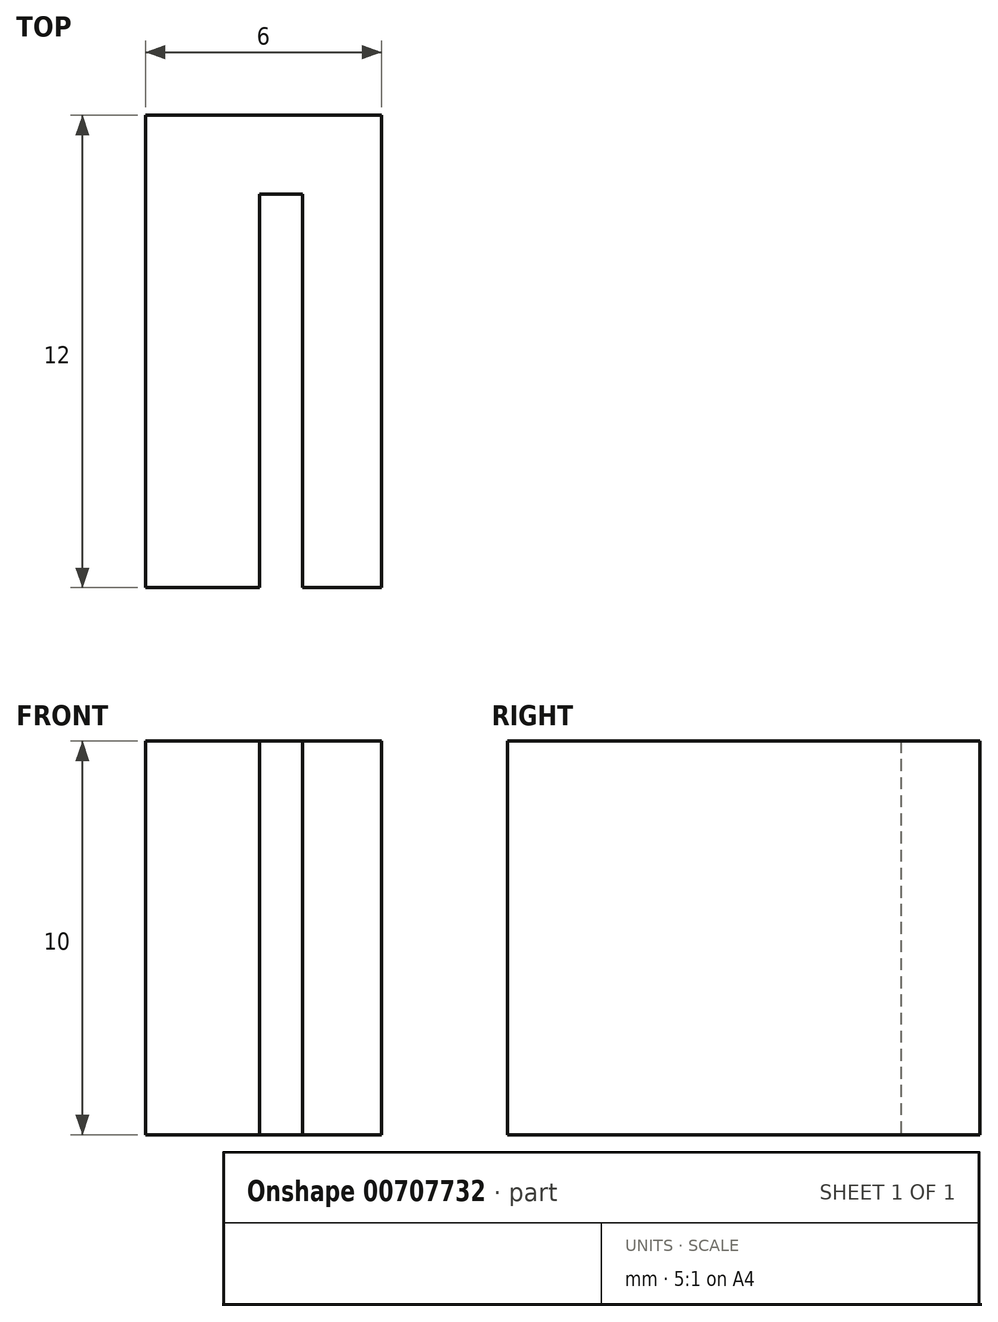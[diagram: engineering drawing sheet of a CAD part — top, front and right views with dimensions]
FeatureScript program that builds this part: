
annotation { "Feature Type Name" : "Feature", "Feature Type Description" : "" }
export const myFeature = defineFeature(function(context is Context, id is Id, definition is map)
    precondition{}
    {
        {
            var Q0;
            Q0=qCreatedBy(makeId("Top.planeOp"),FACE);
            var sketch = newSketch(context, id + "F0", { "sketchPlane" : qUnion([Q0])});
            skLineSegment(sketch, "E0.bottom", {"start": v(0, 0) * mm, "end": v(2.9, 0) * mm});
            skLineSegment(sketch, "E0.top", {"start": v(0, 12) * mm, "end": v(6, 12) * mm});
            skLineSegment(sketch, "E0.left", {"start": v(0, 0) * mm, "end": v(0, 12) * mm});
            skLineSegment(sketch, "E0.right", {"start": v(6, 0) * mm, "end": v(6, 12) * mm});
            skLineSegment(sketch, "E1.top", {"start": v(2.9, 10) * mm, "end": v(4, 10) * mm});
            skLineSegment(sketch, "E1.left", {"start": v(2.9, 0) * mm, "end": v(2.9, 10) * mm});
            skLineSegment(sketch, "E1.right", {"start": v(4, 0) * mm, "end": v(4, 10) * mm});
            skLineSegment(sketch, "E2.trimOffspring", {"start": v(4, 0) * mm, "end": v(6, 0) * mm});
            skSolve(sketch);
        }
        {
            var Q0;
            Q0 = qSketchRegion(id + "F0", true);
            extrude(context, id + "F1", {"entities" : qUnion([Q0]), "depth" : 10 * mm, "offsetDistance" : 25 * mm});
        }
    });
